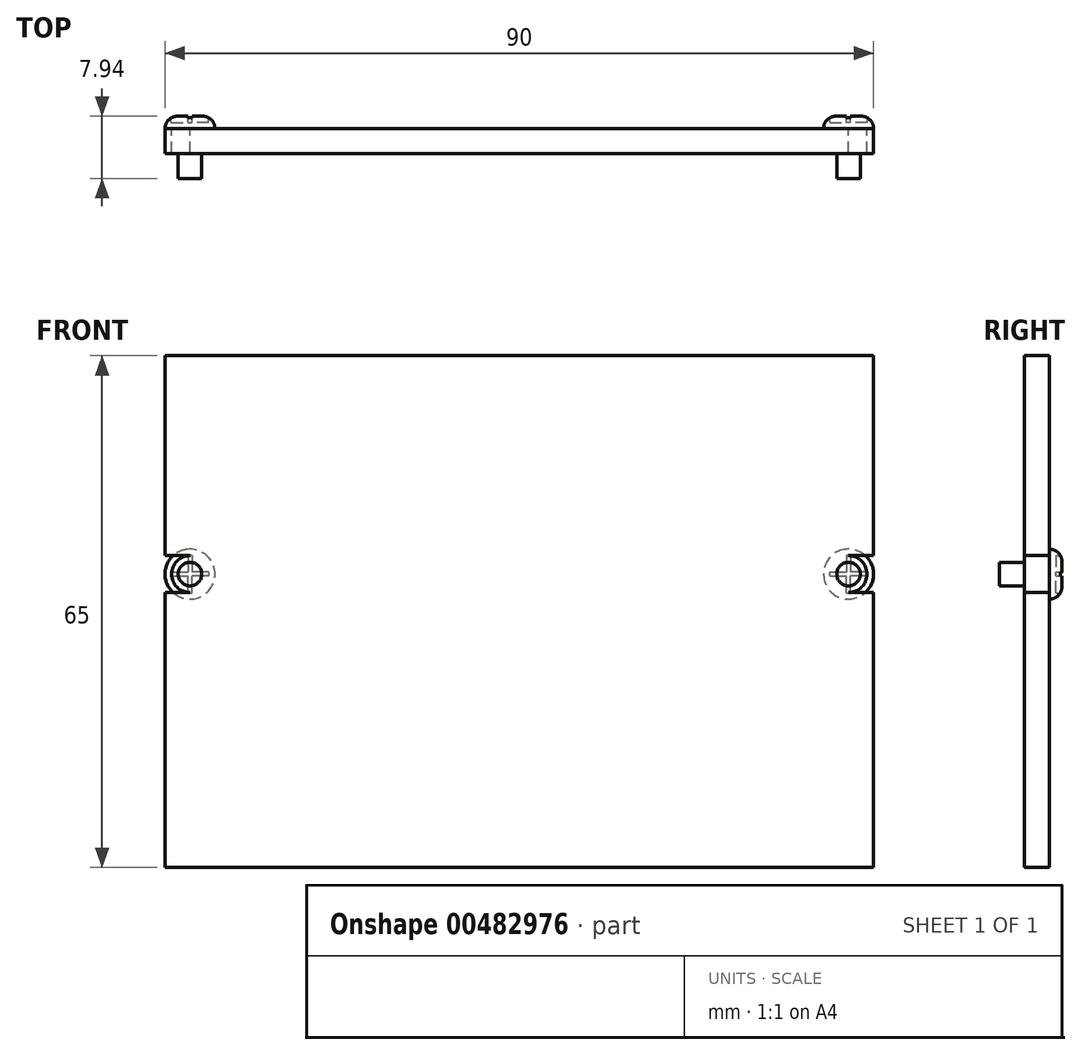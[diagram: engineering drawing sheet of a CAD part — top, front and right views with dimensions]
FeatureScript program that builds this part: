
annotation { "Feature Type Name" : "Feature", "Feature Type Description" : "" }
export const myFeature = defineFeature(function(context is Context, id is Id, definition is map)
    precondition{}
    {
        {
            var Q0;
            Q0=qCreatedBy(makeId("Front.planeOp"),FACE);
            var sketch = newSketch(context, id + "F0", { "sketchPlane" : qUnion([Q0])});
            skLineSegment(sketch, "E0.bottom", {"start": v(-53.08, 50.86) * mm, "end": v(36.92, 50.86) * mm});
            skLineSegment(sketch, "E0.top", {"start": v(-53.08, -14.14) * mm, "end": v(36.92, -14.14) * mm});
            skLineSegment(sketch, "E0.left", {"start": v(-53.08, 50.86) * mm, "end": v(-53.08, 25.46) * mm});
            skLineSegment(sketch, "E0.right", {"start": v(36.92, 50.86) * mm, "end": v(36.92, 25.46) * mm});
            skLineSegment(sketch, "E1", {"start": v(-53.08, 20.78) * mm, "end": v(-49.9, 20.78) * mm});
            skLineSegment(sketch, "E2", {"start": v(-53.08, 25.46) * mm, "end": v(-49.9, 25.46) * mm});
            skArc(sketch, "E3", {"start": v(-49.9, 20.78) * mm, "mid": v(-47.56, 23.12) * mm, "end": v(-49.9, 25.46) * mm});
            skArc(sketch, "E4", {"start": v(33.75, 25.46) * mm, "mid": v(31.41, 23.12) * mm, "end": v(33.75, 20.78) * mm});
            skLineSegment(sketch, "E5.trimOffspring", {"start": v(33.75, 20.78) * mm, "end": v(36.92, 20.78) * mm});
            skLineSegment(sketch, "E6.trimOffspring", {"start": v(-53.08, 20.78) * mm, "end": v(-53.08, -14.14) * mm});
            skLineSegment(sketch, "E7.trimOffspring", {"start": v(33.75, 25.46) * mm, "end": v(36.92, 25.46) * mm});
            skLineSegment(sketch, "E8.trimOffspring", {"start": v(36.92, 20.78) * mm, "end": v(36.92, -14.14) * mm});
            skSolve(sketch);
        }
        {
            var Q0;
            Q0=makeQuery(id+"F0.imprint","IMPRINT",FACE,{"disambiguationData":[TD([[makeQuery(id+"F0.imprint","IMPRINT",EDGE,{"derivedFrom":sQuery(id+"F0.wireOp",EDGE,"E0.bottom")}),-1.0]])]});
            extrude(context, id + "F1", {"entities" : qUnion([Q0]), "depth" : 3.17 * mm});
        }
        {
            var Q0;
            Q0=makeQuery(id+"F1.opExtrude","CAP_FACE",FACE,{"disambiguationData":[OSD([sQuery(id+"F0.wireOp",EDGE,"E0.bottom"),sQuery(id+"F0.wireOp",EDGE,"E0.top"),sQuery(id+"F0.wireOp",EDGE,"E0.left"),sQuery(id+"F0.wireOp",EDGE,"E0.right"),sQuery(id+"F0.wireOp",EDGE,"E1"),sQuery(id+"F0.wireOp",EDGE,"E2"),sQuery(id+"F0.wireOp",EDGE,"E3"),sQuery(id+"F0.wireOp",EDGE,"E4"),sQuery(id+"F0.wireOp",EDGE,"E5.trimOffspring"),sQuery(id+"F0.wireOp",EDGE,"E6.trimOffspring"),sQuery(id+"F0.wireOp",EDGE,"E7.trimOffspring"),sQuery(id+"F0.wireOp",EDGE,"E8.trimOffspring")])],"isStart":true});
            var sketch = newSketch(context, id + "F2", { "sketchPlane" : qUnion([Q0])});
            skCircle(sketch, "E9", {"center": v(-33.75, 23.12) * mm, "radius": 3.17 * mm});
            skCircle(sketch, "E10", {"center": v(49.9, 23.12) * mm, "radius": 3.17 * mm});
            skSolve(sketch);
        }
        {
            var Q0;
            {var subQ5=makeQuery(id+"F1.opExtrude","CAP_EDGE",EDGE,{"disambiguationData":[OSD([sQuery(id+"F0.wireOp",EDGE,"E4")])],"isStart":true});Q0=makeQuery(id+"F2.imprint","IMPRINT",FACE,{"disambiguationData":[TD([[makeQuery(id+"F2.imprint","IMPRINT",EDGE,{"derivedFrom":subQ5}),-1.0]])]});}
            var Q1;
            {var subQ5=makeQuery(id+"F1.opExtrude","CAP_EDGE",EDGE,{"disambiguationData":[OSD([sQuery(id+"F0.wireOp",EDGE,"E4")])],"isStart":true});Q1=makeQuery(id+"F2.imprint","IMPRINT",FACE,{"disambiguationData":[TD([[makeQuery(id+"F2.imprint","IMPRINT",EDGE,{"derivedFrom":subQ5}),1.0]])]});}
            var Q2;
            {var subQ5=makeQuery(id+"F1.opExtrude","CAP_EDGE",EDGE,{"disambiguationData":[OSD([sQuery(id+"F0.wireOp",EDGE,"E3")])],"isStart":true});Q2=makeQuery(id+"F2.imprint","IMPRINT",FACE,{"disambiguationData":[TD([[makeQuery(id+"F2.imprint","IMPRINT",EDGE,{"derivedFrom":subQ5}),-1.0]])]});}
            var Q3;
            {var subQ5=makeQuery(id+"F1.opExtrude","CAP_EDGE",EDGE,{"disambiguationData":[OSD([sQuery(id+"F0.wireOp",EDGE,"E3")])],"isStart":true});Q3=makeQuery(id+"F2.imprint","IMPRINT",FACE,{"disambiguationData":[TD([[makeQuery(id+"F2.imprint","IMPRINT",EDGE,{"derivedFrom":subQ5}),1.0]])]});}
            extrude(context, id + "F3", {"entities" : qUnion([Q0, Q1, Q2, Q3]), "depth" : 1.59 * mm});
        }
        {
            var Q0;
            Q0=makeQuery(id+"F3.opExtrude","CAP_EDGE",EDGE,{"disambiguationData":[OSD([sQuery(id+"F2.wireOp",EDGE,"E9")])],"isStart":false});
            var Q1;
            Q1=makeQuery(id+"F3.opExtrude","CAP_EDGE",EDGE,{"disambiguationData":[OSD([sQuery(id+"F2.wireOp",EDGE,"E10")])],"isStart":false});
            fillet(context, id + "F4", {"entities" : qUnion([Q0, Q1]), "radius" : 1.59 * mm, "tangentPropagation" : true, "allowEdgeOverflow" : false});
        }
        {
            var Q0;
            Q0=makeQuery(id+"F3.opExtrude","CAP_FACE",FACE,{"disambiguationData":[OSD([sQuery(id+"F2.wireOp",EDGE,"E9")])],"isStart":false});
            var sketch = newSketch(context, id + "F5", { "sketchPlane" : qUnion([Q0])});
            skPoint(sketch, "E11", {"position": v(-33.75, 23.12) * mm});
            skLineSegment(sketch, "E12", {"start": v(-33.75, 25.5) * mm, "end": v(-33.5, 25.5) * mm});
            skLineSegment(sketch, "E13", {"start": v(-31.37, 23.12) * mm, "end": v(-31.37, 23.37) * mm});
            skLineSegment(sketch, "E14", {"start": v(-33.5, 25.5) * mm, "end": v(-33.5, 23.37) * mm});
            skLineSegment(sketch, "E15", {"start": v(-31.37, 23.37) * mm, "end": v(-33.5, 23.37) * mm});
            skLineSegment(sketch, "E16.MirrorCS", {"start": v(-36.13, 23.12) * mm, "end": v(-36.13, 23.37) * mm});
            skLineSegment(sketch, "E17.MirrorCS", {"start": v(-36.13, 23.37) * mm, "end": v(-34, 23.37) * mm});
            skLineSegment(sketch, "E18.MirrorCS", {"start": v(-34, 25.5) * mm, "end": v(-34, 23.37) * mm});
            skLineSegment(sketch, "E19.MirrorCS", {"start": v(-33.75, 25.5) * mm, "end": v(-34, 25.5) * mm});
            skLineSegment(sketch, "E20.MirrorCS", {"start": v(-36.13, 23.12) * mm, "end": v(-36.13, 22.87) * mm});
            skLineSegment(sketch, "E21.MirrorCS", {"start": v(-33.75, 20.74) * mm, "end": v(-34, 20.74) * mm});
            skLineSegment(sketch, "E22.MirrorCS", {"start": v(-36.13, 22.87) * mm, "end": v(-34, 22.87) * mm});
            skLineSegment(sketch, "E23.MirrorCS", {"start": v(-34, 20.74) * mm, "end": v(-34, 22.87) * mm});
            skLineSegment(sketch, "E24.MirrorCS", {"start": v(-33.75, 20.74) * mm, "end": v(-33.5, 20.74) * mm});
            skLineSegment(sketch, "E25.MirrorCS", {"start": v(-33.5, 20.74) * mm, "end": v(-33.5, 22.87) * mm});
            skLineSegment(sketch, "E26.MirrorCS", {"start": v(-31.37, 22.87) * mm, "end": v(-33.5, 22.87) * mm});
            skLineSegment(sketch, "E27.MirrorCS", {"start": v(-31.37, 23.12) * mm, "end": v(-31.37, 22.87) * mm});
            skLineSegment(sketch, "E28.MirrorCS", {"start": v(49.9, 20.74) * mm, "end": v(50.15, 20.74) * mm});
            skLineSegment(sketch, "E29.MirrorCS", {"start": v(49.9, 20.74) * mm, "end": v(49.65, 20.74) * mm});
            skLineSegment(sketch, "E30.MirrorCS", {"start": v(52.28, 23.12) * mm, "end": v(52.28, 22.87) * mm});
            skLineSegment(sketch, "E31.MirrorCS", {"start": v(52.28, 23.12) * mm, "end": v(52.28, 23.37) * mm});
            skLineSegment(sketch, "E32.MirrorCS", {"start": v(49.9, 25.5) * mm, "end": v(50.15, 25.5) * mm});
            skLineSegment(sketch, "E33.MirrorCS", {"start": v(49.9, 25.5) * mm, "end": v(49.65, 25.5) * mm});
            skLineSegment(sketch, "E34.MirrorCS", {"start": v(47.52, 23.12) * mm, "end": v(47.52, 22.87) * mm});
            skLineSegment(sketch, "E35.MirrorCS", {"start": v(47.52, 23.12) * mm, "end": v(47.52, 23.37) * mm});
            skLineSegment(sketch, "E36.MirrorCS", {"start": v(47.52, 23.37) * mm, "end": v(49.65, 23.37) * mm});
            skLineSegment(sketch, "E37.MirrorCS", {"start": v(47.52, 22.87) * mm, "end": v(49.65, 22.87) * mm});
            skLineSegment(sketch, "E38.MirrorCS", {"start": v(49.65, 20.74) * mm, "end": v(49.65, 22.87) * mm});
            skLineSegment(sketch, "E39.MirrorCS", {"start": v(50.15, 20.74) * mm, "end": v(50.15, 22.87) * mm});
            skLineSegment(sketch, "E40.MirrorCS", {"start": v(52.28, 22.87) * mm, "end": v(50.15, 22.87) * mm});
            skLineSegment(sketch, "E41.MirrorCS", {"start": v(52.28, 23.37) * mm, "end": v(50.15, 23.37) * mm});
            skLineSegment(sketch, "E42.MirrorCS", {"start": v(49.65, 25.5) * mm, "end": v(49.65, 23.37) * mm});
            skLineSegment(sketch, "E43.MirrorCS", {"start": v(50.15, 25.5) * mm, "end": v(50.15, 23.37) * mm});
            skSolve(sketch);
        }
        {
            var Q0;
            {var subQ0=sQuery(id+"F5.wireOp",EDGE,"E15");var subQ8=sQuery(id+"F5.wireOp",EDGE,"E14");var subQ18=makeQuery(id+"F5.imprint","INTERSECT",VERTEX,{"derivedFrom":[subQ8,subQ0]});Q0=makeQuery(id+"F5.imprint","IMPRINT",FACE,{"disambiguationData":[TD([[makeQuery(id+"F5.imprint","IMPRINT",EDGE,{"disambiguationData":[TD([[subQ18,1.0]])],"derivedFrom":subQ8}),-1.0]])]});}
            var Q1;
            {var subQ1=sQuery(id+"F5.wireOp",EDGE,"E12");Q1=makeQuery(id+"F5.imprint","IMPRINT",FACE,{"disambiguationData":[TD([[makeQuery(id+"F5.imprint","IMPRINT",EDGE,{"derivedFrom":subQ1}),-1.0]])]});}
            var Q2;
            {var subQ1=sQuery(id+"F5.wireOp",EDGE,"E13");Q2=makeQuery(id+"F5.imprint","IMPRINT",FACE,{"disambiguationData":[TD([[makeQuery(id+"F5.imprint","IMPRINT",EDGE,{"derivedFrom":subQ1}),1.0]])]});}
            var Q3;
            {var subQ6=sQuery(id+"F5.wireOp",EDGE,"E21.MirrorCS");Q3=makeQuery(id+"F5.imprint","IMPRINT",FACE,{"disambiguationData":[TD([[makeQuery(id+"F5.imprint","IMPRINT",EDGE,{"derivedFrom":subQ6}),-1.0]])]});}
            var Q4;
            {var subQ6=sQuery(id+"F5.wireOp",EDGE,"E16.MirrorCS");Q4=makeQuery(id+"F5.imprint","IMPRINT",FACE,{"disambiguationData":[TD([[makeQuery(id+"F5.imprint","IMPRINT",EDGE,{"derivedFrom":subQ6}),-1.0]])]});}
            var Q5;
            Q5=makeQuery(id+"F5.imprint","IMPRINT",FACE,{"disambiguationData":[TD([[makeQuery(id+"F5.imprint","IMPRINT",EDGE,{"derivedFrom":sQuery(id+"F5.wireOp",EDGE,"E28.MirrorCS")}),1.0]])]});
            extrude(context, id + "F6", {"entities" : qUnion([Q0, Q1, Q2, Q3, Q4, Q5]), "operationType" : NewBodyOperationType.REMOVE, "oppositeDirection" : true, "depth" : 0.8 * mm});
        }
        {
            var Q0;
            Q0=makeQuery(id+"F3.opExtrude","CAP_FACE",FACE,{"disambiguationData":[OSD([sQuery(id+"F2.wireOp",EDGE,"E9")])],"isStart":true});
            var sketch = newSketch(context, id + "F7", { "sketchPlane" : qUnion([Q0])});
            skCircle(sketch, "E44", {"center": v(33.75, 23.12) * mm, "radius": 2.34 * mm});
            skSolve(sketch);
        }
        {
            var Q0;
            Q0=makeQuery(id+"F3.opExtrude","CAP_FACE",FACE,{"disambiguationData":[OSD([sQuery(id+"F2.wireOp",EDGE,"E10")])],"isStart":true});
            var sketch = newSketch(context, id + "F8", { "sketchPlane" : qUnion([Q0])});
            skCircle(sketch, "E45", {"center": v(-49.9, 23.12) * mm, "radius": 2.34 * mm});
            skSolve(sketch);
        }
        {
            var Q0;
            Q0=makeQuery(id+"F8.imprint","IMPRINT",FACE,{"disambiguationData":[TD([[makeQuery(id+"F8.imprint","IMPRINT",EDGE,{"derivedFrom":sQuery(id+"F8.wireOp",EDGE,"E45")}),1.0]])]});
            var Q1;
            Q1=makeQuery(id+"F7.imprint","IMPRINT",FACE,{"disambiguationData":[TD([[makeQuery(id+"F7.imprint","IMPRINT",EDGE,{"derivedFrom":sQuery(id+"F7.wireOp",EDGE,"E44")}),1.0]])]});
            var Q2;
            Q2=makeQuery(id+"F1.opExtrude","CAP_FACE",FACE,{"disambiguationData":[OSD([sQuery(id+"F0.wireOp",EDGE,"E0.bottom"),sQuery(id+"F0.wireOp",EDGE,"E0.top"),sQuery(id+"F0.wireOp",EDGE,"E0.left"),sQuery(id+"F0.wireOp",EDGE,"E0.right"),sQuery(id+"F0.wireOp",EDGE,"E1"),sQuery(id+"F0.wireOp",EDGE,"E2"),sQuery(id+"F0.wireOp",EDGE,"E3"),sQuery(id+"F0.wireOp",EDGE,"E4"),sQuery(id+"F0.wireOp",EDGE,"E5.trimOffspring"),sQuery(id+"F0.wireOp",EDGE,"E6.trimOffspring"),sQuery(id+"F0.wireOp",EDGE,"E7.trimOffspring"),sQuery(id+"F0.wireOp",EDGE,"E8.trimOffspring")])],"isStart":false});
            extrude(context, id + "F9", {"entities" : qUnion([Q0, Q1]), "operationType" : NewBodyOperationType.ADD, "endBound" : BoundingType.UP_TO_SURFACE, "endBoundEntityFace" : qUnion([Q2]), "depth" : 6.35 * mm});
        }
        {
            var Q0;
            Q0=makeQuery(id+"F9.opExtrude","CAP_FACE",FACE,{"disambiguationData":[OSD([sQuery(id+"F7.wireOp",EDGE,"E44")])],"isStart":false});
            var sketch = newSketch(context, id + "F10", { "sketchPlane" : qUnion([Q0])});
            skCircle(sketch, "E46", {"center": v(33.75, 23.12) * mm, "radius": 1.5 * mm});
            skSolve(sketch);
        }
        {
            var Q0;
            Q0=makeQuery(id+"F9.opExtrude","CAP_FACE",FACE,{"disambiguationData":[OSD([sQuery(id+"F8.wireOp",EDGE,"E45")])],"isStart":false});
            var sketch = newSketch(context, id + "F11", { "sketchPlane" : qUnion([Q0])});
            skCircle(sketch, "E47", {"center": v(-49.9, 23.12) * mm, "radius": 1.5 * mm});
            skSolve(sketch);
        }
        {
            var Q0;
            Q0=makeQuery(id+"F11.imprint","IMPRINT",FACE,{"disambiguationData":[TD([[makeQuery(id+"F11.imprint","IMPRINT",EDGE,{"derivedFrom":sQuery(id+"F11.wireOp",EDGE,"E47")}),1.0]])]});
            var Q1;
            Q1=makeQuery(id+"F10.imprint","IMPRINT",FACE,{"disambiguationData":[TD([[makeQuery(id+"F10.imprint","IMPRINT",EDGE,{"derivedFrom":sQuery(id+"F10.wireOp",EDGE,"E46")}),1.0]])]});
            extrude(context, id + "F12", {"entities" : qUnion([Q0, Q1]), "operationType" : NewBodyOperationType.ADD, "depth" : 3.17 * mm});
        }
    });
